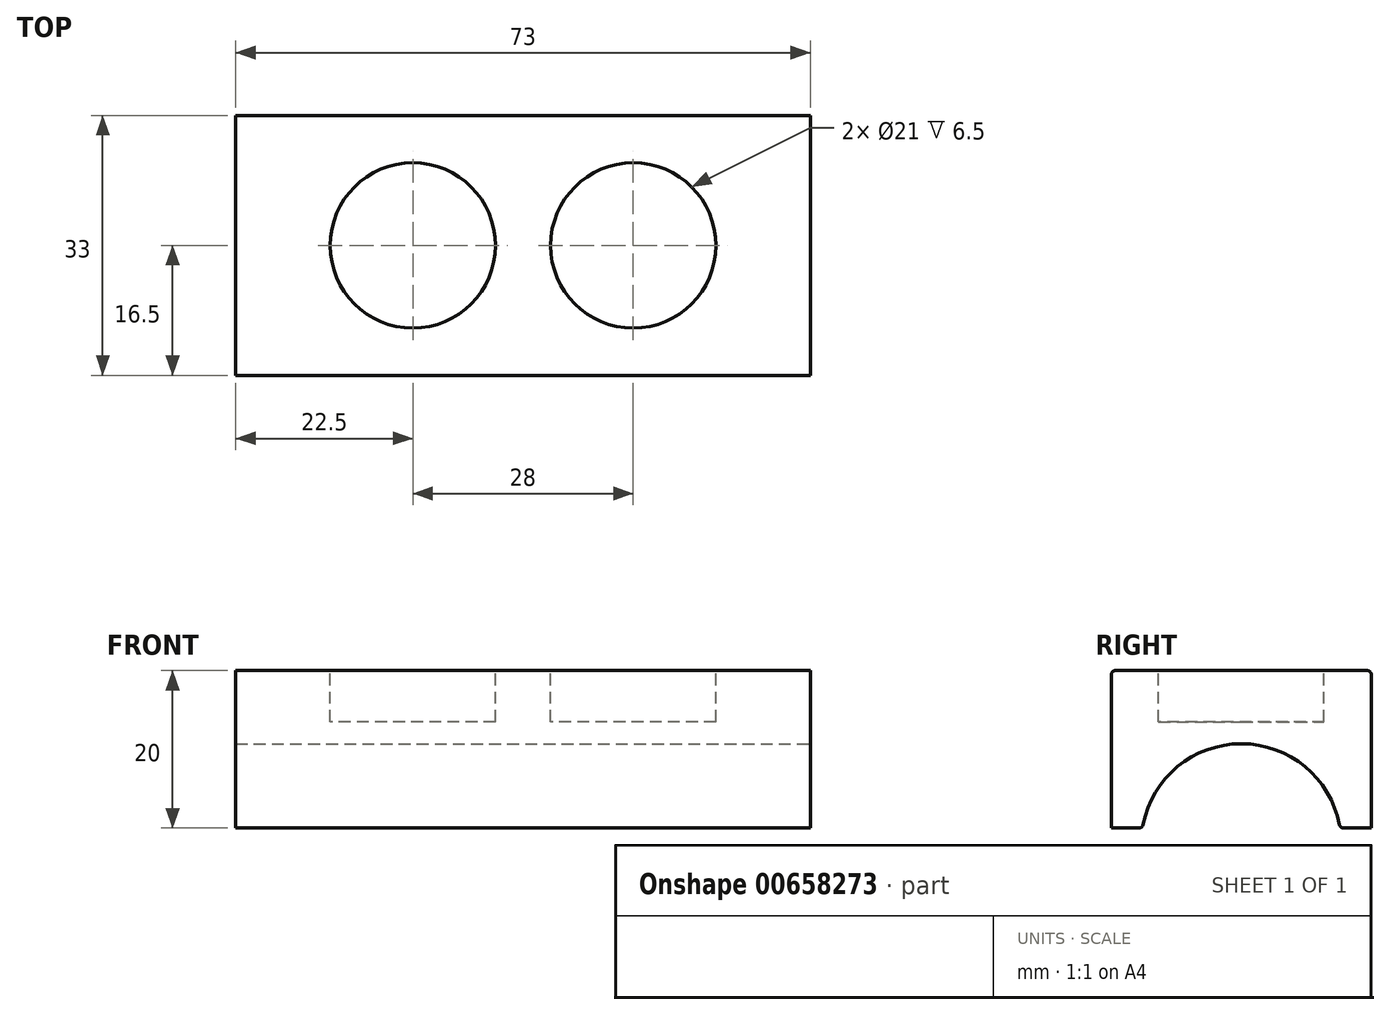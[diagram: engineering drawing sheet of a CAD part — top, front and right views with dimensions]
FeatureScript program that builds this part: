
annotation { "Feature Type Name" : "Feature", "Feature Type Description" : "" }
export const myFeature = defineFeature(function(context is Context, id is Id, definition is map)
    precondition{}
    {
        {
            var Q0;
            Q0=qCreatedBy(makeId("Top.planeOp"),FACE);
            var sketch = newSketch(context, id + "F0", { "sketchPlane" : qUnion([Q0])});
            skLineSegment(sketch, "E0.bottom", {"start": v(36.5, -16.5) * mm, "end": v(-36.5, -16.5) * mm});
            skLineSegment(sketch, "E0.top", {"start": v(36.5, 16.5) * mm, "end": v(-36.5, 16.5) * mm});
            skLineSegment(sketch, "E0.left", {"start": v(36.5, -16.5) * mm, "end": v(36.5, 16.5) * mm});
            skLineSegment(sketch, "E0.right", {"start": v(-36.5, -16.5) * mm, "end": v(-36.5, 16.5) * mm});
            skPoint(sketch, "E0.middle", {"position": v(0, 0) * mm});
            skSolve(sketch);
        }
        {
            var Q0;
            Q0=makeQuery(id+"F0.imprint","IMPRINT",FACE,{"disambiguationData":[TD([[makeQuery(id+"F0.imprint","IMPRINT",EDGE,{"derivedFrom":sQuery(id+"F0.wireOp",EDGE,"E0.bottom")}),-1.0]])]});
            extrude(context, id + "F1", {"entities" : qUnion([Q0]), "depth" : 20 * mm, "offsetDistance" : 25.4 * mm});
        }
        {
            var Q0;
            Q0=makeQuery(id+"F1.opExtrude","CAP_FACE",FACE,{"disambiguationData":[OSD([sQuery(id+"F0.wireOp",EDGE,"E0.bottom"),sQuery(id+"F0.wireOp",EDGE,"E0.top"),sQuery(id+"F0.wireOp",EDGE,"E0.left"),sQuery(id+"F0.wireOp",EDGE,"E0.right")])],"isStart":false});
            var sketch = newSketch(context, id + "F2", { "sketchPlane" : qUnion([Q0])});
            skCircle(sketch, "E1", {"center": v(-14, 0) * mm, "radius": 10.5 * mm});
            skCircle(sketch, "E2", {"center": v(14, 0) * mm, "radius": 10.5 * mm});
            skLineSegment(sketch, "E3", {"start": v(-14, 0) * mm, "end": v(14, 0) * mm, "construction": true});
            skLineSegment(sketch, "E4", {"start": v(0, -16.5) * mm, "end": v(0, 0) * mm, "construction": true});
            skSolve(sketch);
        }
        {
            var Q0;
            Q0=makeQuery(id+"F2.imprint","IMPRINT",FACE,{"disambiguationData":[TD([[makeQuery(id+"F2.imprint","IMPRINT",EDGE,{"derivedFrom":sQuery(id+"F2.wireOp",EDGE,"E1")}),1.0]])]});
            var Q1;
            Q1=makeQuery(id+"F2.imprint","IMPRINT",FACE,{"disambiguationData":[TD([[makeQuery(id+"F2.imprint","IMPRINT",EDGE,{"derivedFrom":sQuery(id+"F2.wireOp",EDGE,"E2")}),1.0]])]});
            extrude(context, id + "F3", {"entities" : qUnion([Q0, Q1]), "operationType" : NewBodyOperationType.REMOVE, "oppositeDirection" : true, "depth" : 6.5 * mm, "offsetDistance" : 25.4 * mm});
        }
        {
            var Q0;
            Q0=makeQuery(id+"F1.opExtrude","SWEPT_FACE",FACE,{"disambiguationData":[OSD([sQuery(id+"F0.wireOp",EDGE,"E0.left")])]});
            var sketch = newSketch(context, id + "F4", { "sketchPlane" : qUnion([Q0])});
            skCircle(sketch, "E5", {"center": v(0, -2) * mm, "radius": 12.7 * mm});
            skLineSegment(sketch, "E6", {"start": v(0, 0) * mm, "end": v(0, -2) * mm, "construction": true});
            skSolve(sketch);
        }
        {
            var Q0;
            {var subQ0=sQuery(id+"F4.wireOp",EDGE,"E5");var subQ1=makeQuery(id+"F1.opExtrude","CAP_EDGE",EDGE,{"disambiguationData":[OSD([sQuery(id+"F0.wireOp",EDGE,"E0.left")])],"isStart":true});var subQ2=makeQuery(id+"F4.imprint","INTERSECT",VERTEX,{"disambiguationData":[OD(0.0)],"derivedFrom":[subQ1,subQ0]});Q0=makeQuery(id+"F4.imprint","IMPRINT",FACE,{"disambiguationData":[TD([[makeQuery(id+"F4.imprint","IMPRINT",EDGE,{"disambiguationData":[TD([[subQ2,1.0]])],"derivedFrom":subQ0}),1.0]])]});}
            var Q1;
            {var subQ0=sQuery(id+"F4.wireOp",EDGE,"E5");var subQ1=makeQuery(id+"F1.opExtrude","CAP_EDGE",EDGE,{"disambiguationData":[OSD([sQuery(id+"F0.wireOp",EDGE,"E0.left")])],"isStart":true});var subQ2=makeQuery(id+"F4.imprint","INTERSECT",VERTEX,{"disambiguationData":[OD(0.0)],"derivedFrom":[subQ1,subQ0]});Q1=makeQuery(id+"F4.imprint","IMPRINT",FACE,{"disambiguationData":[TD([[makeQuery(id+"F4.imprint","IMPRINT",EDGE,{"disambiguationData":[TD([[subQ2,-1.0]])],"derivedFrom":subQ0}),1.0]])]});}
            extrude(context, id + "F5", {"entities" : qUnion([Q0, Q1]), "operationType" : NewBodyOperationType.REMOVE, "endBound" : BoundingType.THROUGH_ALL, "oppositeDirection" : true, "depth" : 25.4 * mm, "offsetDistance" : 25.4 * mm});
        }
        {
            var Q0;
            Q0=makeQuery(id+"F1.opExtrude","CAP_EDGE",EDGE,{"disambiguationData":[OSD([sQuery(id+"F0.wireOp",EDGE,"E0.top")])],"isStart":false});
            var Q1;
            Q1=makeQuery(id+"F1.opExtrude","CAP_EDGE",EDGE,{"disambiguationData":[OSD([sQuery(id+"F0.wireOp",EDGE,"E0.bottom")])],"isStart":false});
            var Q2;
            Q2=makeQuery(id+"F5.boolean.opBoolean","INTERSECT",EDGE,{"disambiguationData":[OD(0.0)],"derivedFrom":[makeQuery(id+"F1.opExtrude","CAP_FACE",FACE,{"disambiguationData":[OSD([sQuery(id+"F0.wireOp",EDGE,"E0.bottom"),sQuery(id+"F0.wireOp",EDGE,"E0.top"),sQuery(id+"F0.wireOp",EDGE,"E0.left"),sQuery(id+"F0.wireOp",EDGE,"E0.right")])],"isStart":true}),makeQuery(id+"F5.opExtrude","SWEPT_FACE",FACE,{"disambiguationData":[OSD([sQuery(id+"F4.wireOp",EDGE,"E5")])]})]});
            var Q3;
            Q3=makeQuery(id+"F5.boolean.opBoolean","INTERSECT",EDGE,{"disambiguationData":[OD(1.0)],"derivedFrom":[makeQuery(id+"F1.opExtrude","CAP_FACE",FACE,{"disambiguationData":[OSD([sQuery(id+"F0.wireOp",EDGE,"E0.bottom"),sQuery(id+"F0.wireOp",EDGE,"E0.top"),sQuery(id+"F0.wireOp",EDGE,"E0.left"),sQuery(id+"F0.wireOp",EDGE,"E0.right")])],"isStart":true}),makeQuery(id+"F5.opExtrude","SWEPT_FACE",FACE,{"disambiguationData":[OSD([sQuery(id+"F4.wireOp",EDGE,"E5")])]})]});
            fillet(context, id + "F6", {"entities" : qUnion([Q0, Q1, Q2, Q3]), "radius" : 0.5 * mm, "tangentPropagation" : true, "allowEdgeOverflow" : false});
        }
    });
